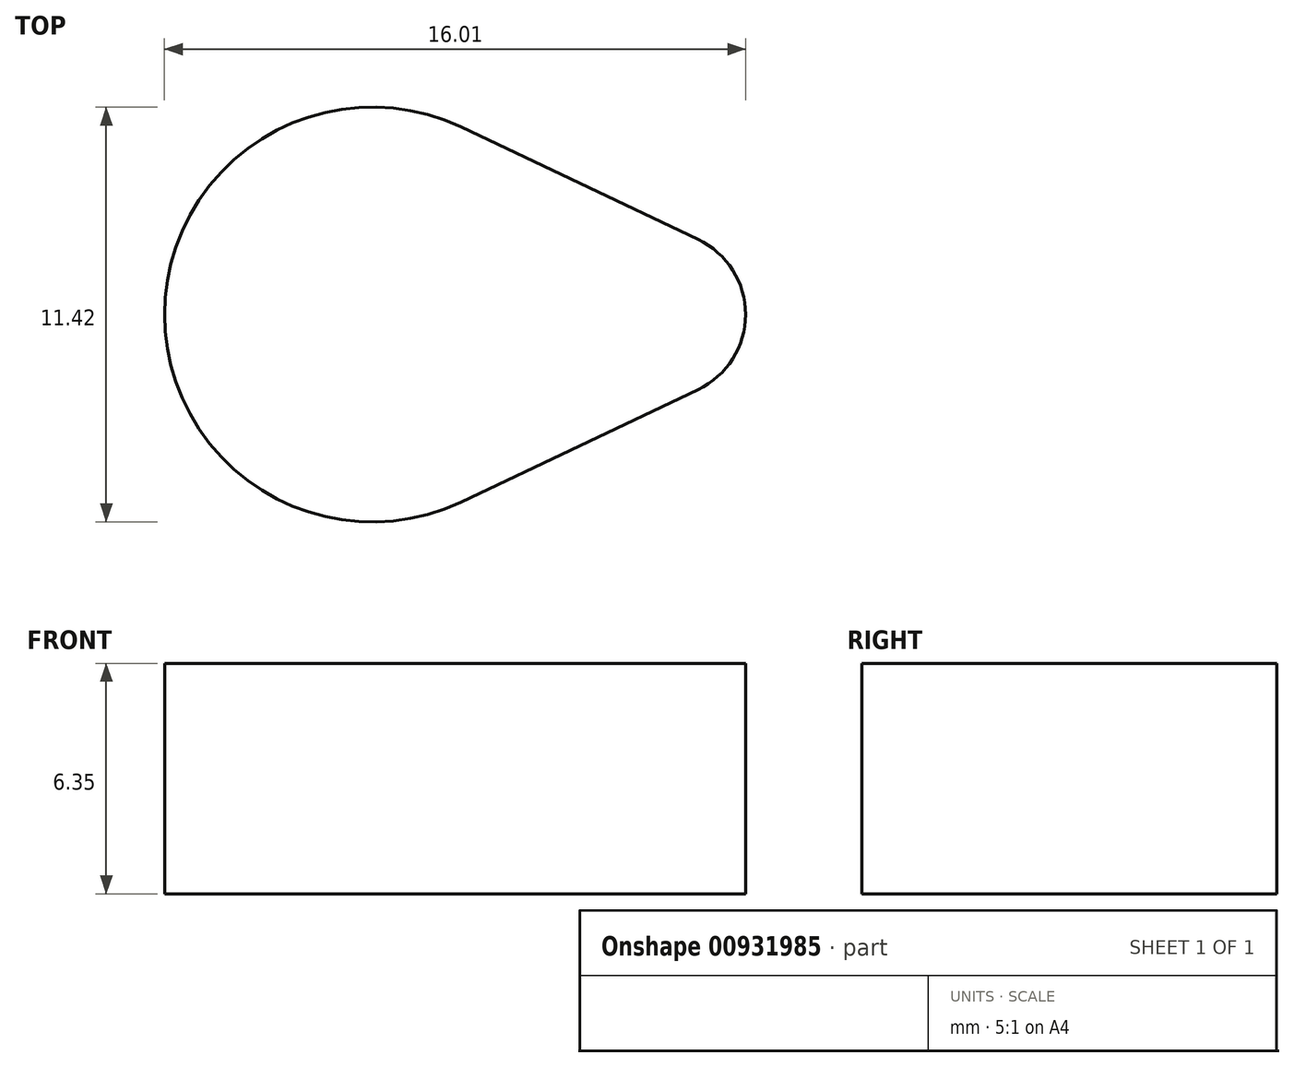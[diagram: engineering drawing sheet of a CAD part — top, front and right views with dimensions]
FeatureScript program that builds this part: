
annotation { "Feature Type Name" : "Feature", "Feature Type Description" : "" }
export const myFeature = defineFeature(function(context is Context, id is Id, definition is map)
    precondition{}
    {
        {
            var Q0;
            Q0=qCreatedBy(makeId("Top.planeOp"),FACE);
            var sketch = newSketch(context, id + "F0", { "sketchPlane" : qUnion([Q0])});
            skArc(sketch, "E0", {"start": v(2.45, 5.16) * mm, "mid": v(-3.05, 4.83) * mm, "end": v(-5.71, 0) * mm});
            skArc(sketch, "E1", {"start": v(10.29, 0) * mm, "mid": v(9.93, 1.22) * mm, "end": v(8.98, 2.07) * mm});
            skLineSegment(sketch, "E2", {"start": v(2.45, 5.16) * mm, "end": v(8.98, 2.07) * mm});
            skArc(sketch, "E3.MirrorCS", {"start": v(2.45, -5.16) * mm, "mid": v(-3.05, -4.83) * mm, "end": v(-5.71, 0) * mm});
            skLineSegment(sketch, "E4.MirrorCS", {"start": v(2.45, -5.16) * mm, "end": v(8.98, -2.07) * mm});
            skArc(sketch, "E5.MirrorCS", {"start": v(10.29, 0) * mm, "mid": v(9.93, -1.22) * mm, "end": v(8.98, -2.07) * mm});
            skSolve(sketch);
        }
        {
            var Q0;
            Q0=makeQuery(id+"F0.imprint","IMPRINT",FACE,{"disambiguationData":[TD([[makeQuery(id+"F0.imprint","IMPRINT",EDGE,{"derivedFrom":sQuery(id+"F0.wireOp",EDGE,"E0")}),1.0]])]});
            extrude(context, id + "F1", {"entities" : qUnion([Q0]), "oppositeDirection" : true, "depth" : 6.35 * mm, "offsetDistance" : 25.4 * mm});
        }
    });
